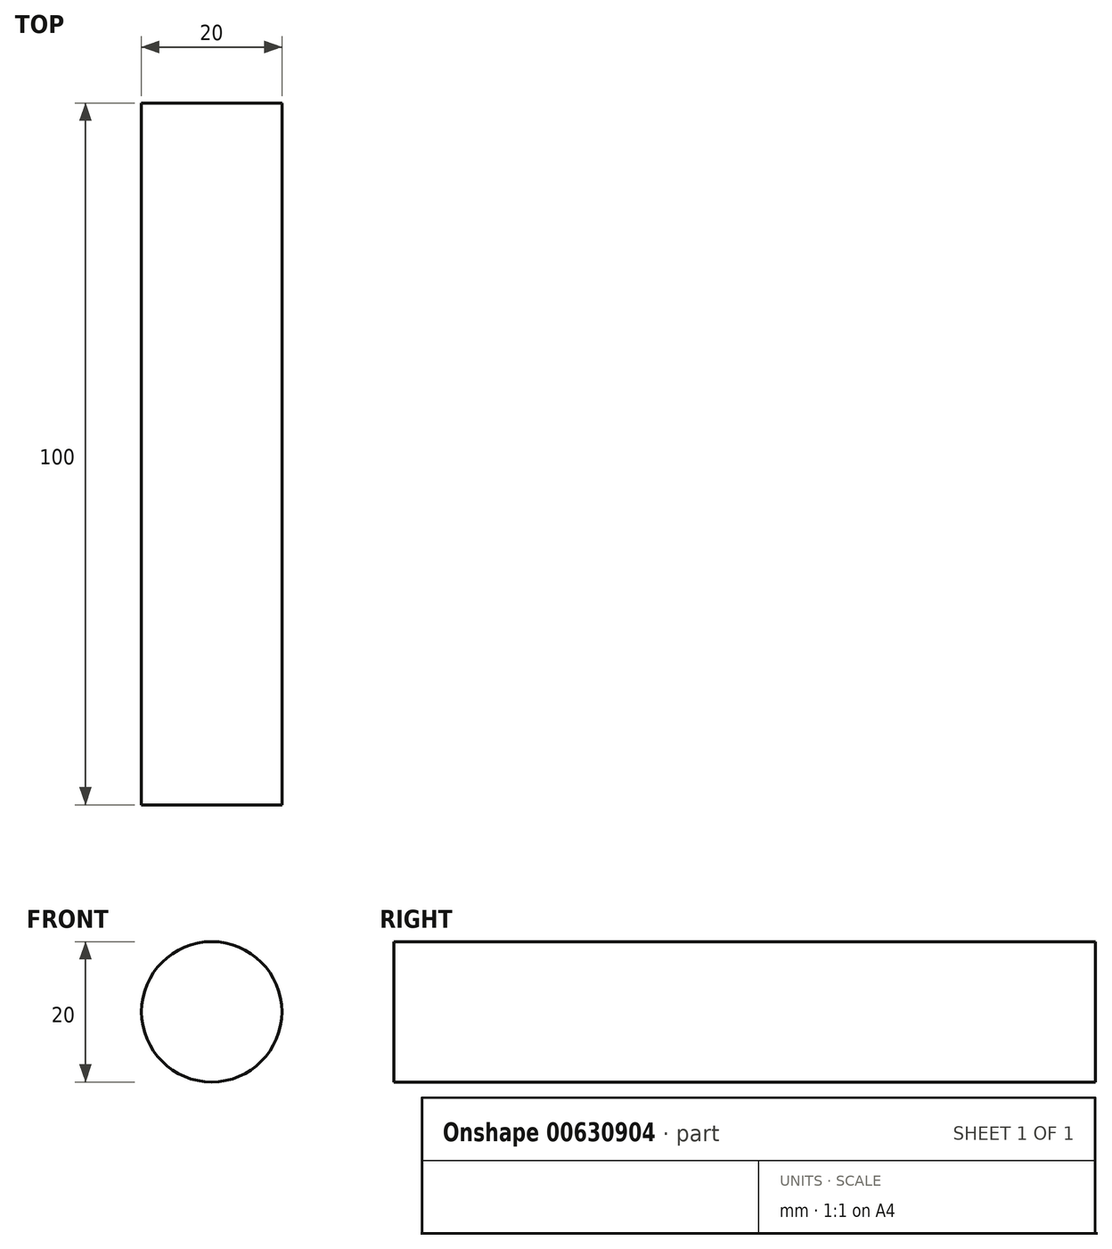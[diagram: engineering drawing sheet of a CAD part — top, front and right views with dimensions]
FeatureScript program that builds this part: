
annotation { "Feature Type Name" : "Feature", "Feature Type Description" : "" }
export const myFeature = defineFeature(function(context is Context, id is Id, definition is map)
    precondition{}
    {
        {
            var Q0;
            Q0=qCreatedBy(makeId("Right.planeOp"),FACE);
            var sketch = newSketch(context, id + "F0", { "sketchPlane" : qUnion([Q0])});
            skLineSegment(sketch, "E0", {"start": v(0, 0) * mm, "end": v(200, 0) * mm});
            skLineSegment(sketch, "E1", {"start": v(200, 0) * mm, "end": v(0, 0) * mm});
            skLineSegment(sketch, "E2", {"start": v(-100, 0) * mm, "end": v(0, 0) * mm});
            skLineSegment(sketch, "E3", {"start": v(0, 10) * mm, "end": v(0, 0) * mm});
            skLineSegment(sketch, "E4", {"start": v(0, 10) * mm, "end": v(200, 0) * mm});
            skLineSegment(sketch, "E5", {"start": v(-100, 0) * mm, "end": v(-100, 10) * mm});
            skLineSegment(sketch, "E6", {"start": v(-100, 10) * mm, "end": v(0, 10) * mm});
            skSolve(sketch);
        }
        {
            var Q0;
            Q0=makeQuery(id+"F0.imprint","IMPRINT",FACE,{"disambiguationData":[TD([[makeQuery(id+"F0.imprint","IMPRINT",EDGE,{"derivedFrom":sQuery(id+"F0.wireOp",EDGE,"E1")}),-1.0]])]});
            var Q1;
            Q1=makeQuery(id+"F0.imprint","IMPRINT",FACE,{"disambiguationData":[TD([[makeQuery(id+"F0.imprint","IMPRINT",EDGE,{"derivedFrom":sQuery(id+"F0.wireOp",EDGE,"E2")}),1.0]])]});
            var Q2;
            Q2=sQuery(id+"F0.wireOp",EDGE,"E0");
            revolve(context, id + "F1", {"entities" : qUnion([Q0, Q1]), "axis" : qUnion([Q2]), "revolveType" : RevolveType.FULL});
        }
    });
